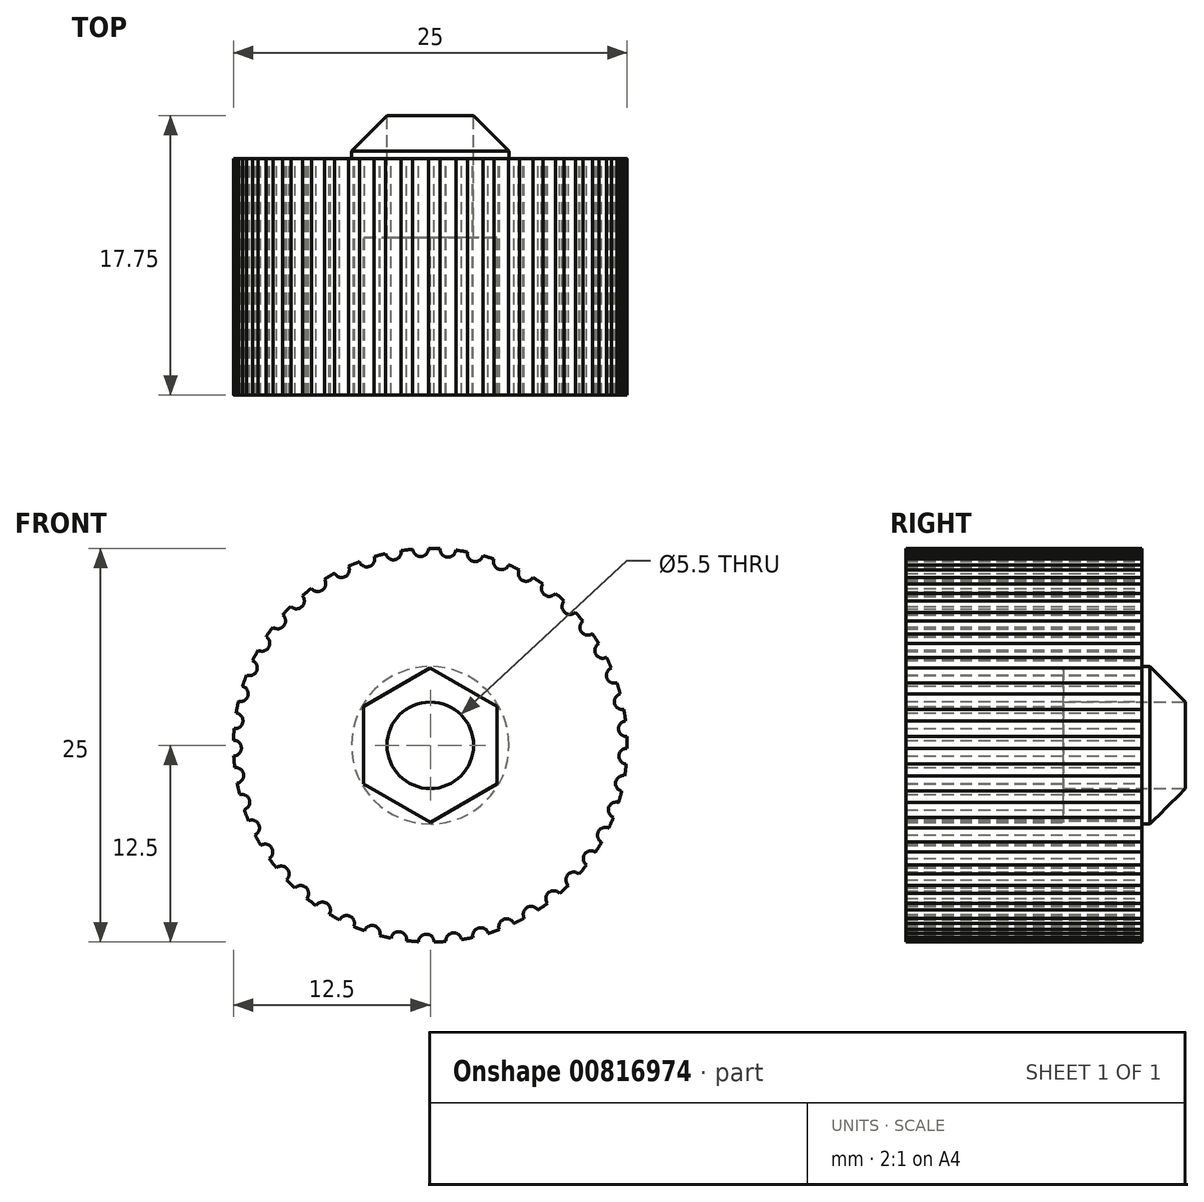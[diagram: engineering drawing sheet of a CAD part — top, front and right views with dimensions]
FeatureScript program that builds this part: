
annotation { "Feature Type Name" : "Feature", "Feature Type Description" : "" }
export const myFeature = defineFeature(function(context is Context, id is Id, definition is map)
    precondition{}
    {
        {
            var Q0;
            Q0=qCreatedBy(makeId("Front.planeOp"),FACE);
            var sketch = newSketch(context, id + "F0", { "sketchPlane" : qUnion([Q0])});
            skCircle(sketch, "E0.cCircle", {"center": v(0, 0) * mm, "radius": 4.25 * mm, "construction": true});
            skLineSegment(sketch, "E0.0", {"start": v(-4.25, 2.45) * mm, "end": v(0, 4.9) * mm});
            skLineSegment(sketch, "E0.1", {"start": v(0, 4.9) * mm, "end": v(4.25, 2.46) * mm});
            skLineSegment(sketch, "E0.2", {"start": v(4.25, 2.46) * mm, "end": v(4.25, -2.45) * mm});
            skLineSegment(sketch, "E0.3", {"start": v(4.25, -2.45) * mm, "end": v(0, -4.9) * mm});
            skLineSegment(sketch, "E0.4", {"start": v(0, -4.9) * mm, "end": v(-4.25, -2.46) * mm});
            skLineSegment(sketch, "E0.5", {"start": v(-4.25, -2.46) * mm, "end": v(-4.25, 2.45) * mm});
            skPoint(sketch, "E0.0.midPoint", {"position": v(-2.13, 3.68) * mm});
            skCircle(sketch, "E1", {"center": v(0, 0) * mm, "radius": 2.75 * mm});
            skCircle(sketch, "E2", {"center": v(0, 0) * mm, "radius": 12.5 * mm});
            skCircle(sketch, "E3", {"center": v(0, 0) * mm, "radius": 5 * mm});
            skSolve(sketch);
        }
        {
            var Q0;
            Q0=makeQuery(id+"F0.imprint","IMPRINT",FACE,{"disambiguationData":[TD([[makeQuery(id+"F0.imprint","IMPRINT",EDGE,{"derivedFrom":sQuery(id+"F0.wireOp",EDGE,"E2")}),1.0]])]});
            extrude(context, id + "F1", {"entities" : qUnion([Q0]), "depth" : 15 * mm, "offsetDistance" : 25 * mm});
        }
        {
            var Q0;
            Q0=makeQuery(id+"F0.imprint","IMPRINT",FACE,{"disambiguationData":[TD([[makeQuery(id+"F0.imprint","IMPRINT",EDGE,{"derivedFrom":sQuery(id+"F0.wireOp",EDGE,"E0.0")}),1.0]])]});
            extrude(context, id + "F2", {"entities" : qUnion([Q0]), "operationType" : NewBodyOperationType.ADD, "depth" : 15 * mm, "offsetDistance" : 25 * mm});
        }
        {
            var Q0;
            Q0=makeQuery(id+"F0.imprint","IMPRINT",FACE,{"disambiguationData":[TD([[makeQuery(id+"F0.imprint","IMPRINT",EDGE,{"derivedFrom":sQuery(id+"F0.wireOp",EDGE,"E0.0")}),-1.0]])]});
            extrude(context, id + "F3", {"entities" : qUnion([Q0]), "operationType" : NewBodyOperationType.ADD, "depth" : 5 * mm, "offsetDistance" : 25 * mm});
        }
        {
            var Q0;
            Q0=makeQuery(id+"F0.imprint","IMPRINT",FACE,{"disambiguationData":[TD([[makeQuery(id+"F0.imprint","IMPRINT",EDGE,{"derivedFrom":sQuery(id+"F0.wireOp",EDGE,"E0.0")}),1.0]])]});
            extrude(context, id + "F4", {"entities" : qUnion([Q0]), "operationType" : NewBodyOperationType.ADD, "oppositeDirection" : true, "depth" : 3 * mm, "offsetDistance" : 25 * mm});
        }
        {
            var Q0;
            Q0=makeQuery(id+"F0.imprint","IMPRINT",FACE,{"disambiguationData":[TD([[makeQuery(id+"F0.imprint","IMPRINT",EDGE,{"derivedFrom":sQuery(id+"F0.wireOp",EDGE,"E0.0")}),-1.0]])]});
            extrude(context, id + "F5", {"entities" : qUnion([Q0]), "operationType" : NewBodyOperationType.ADD, "oppositeDirection" : true, "depth" : 3 * mm, "offsetDistance" : 25 * mm});
        }
        {
            var Q0;
            Q0=makeQuery(id+"F4.opExtrude","CAP_EDGE",EDGE,{"disambiguationData":[OSD([sQuery(id+"F0.wireOp",EDGE,"E3")])],"isStart":false});
            chamfer(context, id + "F6", {"entities" : qUnion([Q0]), "width" : 2.5 * mm, "tangentPropagation" : true});
        }
        {
            var Q0;
            Q0=qCreatedBy(makeId("Front.planeOp"),FACE);
            var sketch = newSketch(context, id + "F7", { "sketchPlane" : qUnion([Q0])});
            skCircle(sketch, "E4", {"center": v(-5.32, -11.31) * mm, "radius": 0.5 * mm});
            skCircle(sketch, "E5.1.0", {"center": v(-3.7, -11.94) * mm, "radius": 0.5 * mm});
            skCircle(sketch, "E5.2.0", {"center": v(-2, -12.34) * mm, "radius": 0.5 * mm});
            skCircle(sketch, "E5.3.0", {"center": v(-0.26, -12.5) * mm, "radius": 0.5 * mm});
            skCircle(sketch, "E5.4.0", {"center": v(1.48, -12.41) * mm, "radius": 0.5 * mm});
            skCircle(sketch, "E5.5.0", {"center": v(3.2, -12.08) * mm, "radius": 0.5 * mm});
            skCircle(sketch, "E5.6.0", {"center": v(4.85, -11.52) * mm, "radius": 0.5 * mm});
            skCircle(sketch, "E5.7.0", {"center": v(6.4, -10.73) * mm, "radius": 0.5 * mm});
            skCircle(sketch, "E5.8.0", {"center": v(7.84, -9.74) * mm, "radius": 0.5 * mm});
            skCircle(sketch, "E5.9.0", {"center": v(9.12, -8.55) * mm, "radius": 0.5 * mm});
            skCircle(sketch, "E5.10.0", {"center": v(10.22, -7.2) * mm, "radius": 0.5 * mm});
            skCircle(sketch, "E5.11.0", {"center": v(11.12, -5.7) * mm, "radius": 0.5 * mm});
            skCircle(sketch, "E5.12.0", {"center": v(11.8, -4.1) * mm, "radius": 0.5 * mm});
            skCircle(sketch, "E5.13.0", {"center": v(12.26, -2.42) * mm, "radius": 0.5 * mm});
            skCircle(sketch, "E5.14.0", {"center": v(12.48, -0.7) * mm, "radius": 0.5 * mm});
            skCircle(sketch, "E5.15.0", {"center": v(12.46, 1.05) * mm, "radius": 0.5 * mm});
            skCircle(sketch, "E5.16.0", {"center": v(12.19, 2.77) * mm, "radius": 0.5 * mm});
            skCircle(sketch, "E5.17.0", {"center": v(11.68, 4.44) * mm, "radius": 0.5 * mm});
            skCircle(sketch, "E5.18.0", {"center": v(10.95, 6.03) * mm, "radius": 0.5 * mm});
            skCircle(sketch, "E5.19.0", {"center": v(10, 7.5) * mm, "radius": 0.5 * mm});
            skCircle(sketch, "E5.20.0", {"center": v(8.87, 8.81) * mm, "radius": 0.5 * mm});
            skCircle(sketch, "E5.21.0", {"center": v(7.55, 9.96) * mm, "radius": 0.5 * mm});
            skCircle(sketch, "E5.22.0", {"center": v(6.1, 10.91) * mm, "radius": 0.5 * mm});
            skCircle(sketch, "E5.23.0", {"center": v(4.52, 11.66) * mm, "radius": 0.5 * mm});
            skCircle(sketch, "E5.24.0", {"center": v(2.85, 12.17) * mm, "radius": 0.5 * mm});
            skCircle(sketch, "E5.25.0", {"center": v(1.13, 12.45) * mm, "radius": 0.5 * mm});
            skCircle(sketch, "E5.26.0", {"center": v(-0.61, 12.48) * mm, "radius": 0.5 * mm});
            skCircle(sketch, "E5.27.0", {"center": v(-2.35, 12.28) * mm, "radius": 0.5 * mm});
            skCircle(sketch, "E5.28.0", {"center": v(-4.03, 11.83) * mm, "radius": 0.5 * mm});
            skCircle(sketch, "E5.29.0", {"center": v(-5.64, 11.16) * mm, "radius": 0.5 * mm});
            skCircle(sketch, "E5.30.0", {"center": v(-7.14, 10.26) * mm, "radius": 0.5 * mm});
            skCircle(sketch, "E5.31.0", {"center": v(-8.5, 9.17) * mm, "radius": 0.5 * mm});
            skCircle(sketch, "E5.32.0", {"center": v(-9.69, 7.9) * mm, "radius": 0.5 * mm});
            skCircle(sketch, "E5.33.0", {"center": v(-10.7, 6.47) * mm, "radius": 0.5 * mm});
            skCircle(sketch, "E5.34.0", {"center": v(-11.5, 4.92) * mm, "radius": 0.5 * mm});
            skCircle(sketch, "E5.35.0", {"center": v(-12.06, 3.27) * mm, "radius": 0.5 * mm});
            skCircle(sketch, "E5.36.0", {"center": v(-12.4, 1.56) * mm, "radius": 0.5 * mm});
            skCircle(sketch, "E5.37.0", {"center": v(-12.5, -0.18) * mm, "radius": 0.5 * mm});
            skCircle(sketch, "E5.38.0", {"center": v(-12.35, -1.92) * mm, "radius": 0.5 * mm});
            skCircle(sketch, "E5.39.0", {"center": v(-11.97, -3.62) * mm, "radius": 0.5 * mm});
            skCircle(sketch, "E5.40.0", {"center": v(-11.35, -5.25) * mm, "radius": 0.5 * mm});
            skCircle(sketch, "E5.41.0", {"center": v(-10.5, -6.77) * mm, "radius": 0.5 * mm});
            skCircle(sketch, "E5.42.0", {"center": v(-9.46, -8.17) * mm, "radius": 0.5 * mm});
            skCircle(sketch, "E5.43.0", {"center": v(-8.23, -9.4) * mm, "radius": 0.5 * mm});
            skCircle(sketch, "E5.44.0", {"center": v(-6.84, -10.46) * mm, "radius": 0.5 * mm});
            skPoint(sketch, "E5.center", {"position": v(0, 0) * mm});
            skSolve(sketch);
        }
        {
            var Q0;
            Q0 = qSketchRegion(id + "F7", true);
            extrude(context, id + "F8", {"entities" : qUnion([Q0]), "operationType" : NewBodyOperationType.REMOVE, "depth" : 15 * mm, "offsetDistance" : 25 * mm});
        }
    });
